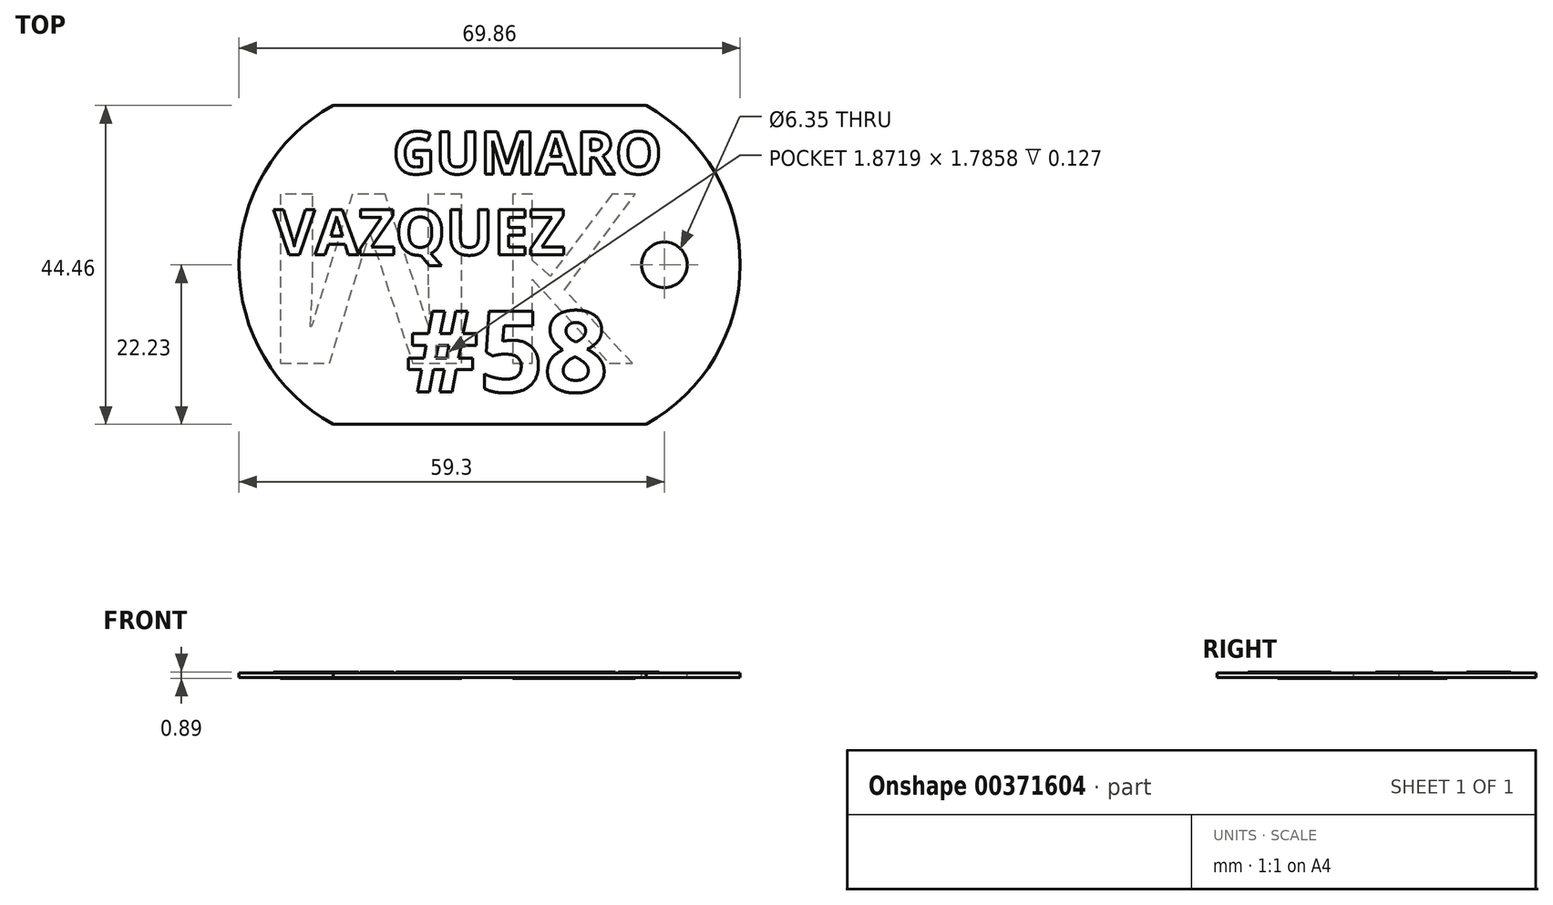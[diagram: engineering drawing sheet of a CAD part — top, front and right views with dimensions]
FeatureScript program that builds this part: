
annotation { "Feature Type Name" : "Feature", "Feature Type Description" : "" }
export const myFeature = defineFeature(function(context is Context, id is Id, definition is map)
    precondition{}
    {
        {
            var Q0;
            Q0=qCreatedBy(makeId("Top.planeOp"),FACE);
            var sketch = newSketch(context, id + "F0", { "sketchPlane" : qUnion([Q0])});
            skLineSegment(sketch, "E0.bottom", {"start": v(21.82, -22.22) * mm, "end": v(-21.82, -22.23) * mm});
            skLineSegment(sketch, "E0.top", {"start": v(21.82, 22.23) * mm, "end": v(-21.82, 22.23) * mm});
            skPoint(sketch, "E0.middle", {"position": v(0, 0) * mm});
            skArc(sketch, "E1", {"start": v(-21.82, 22.22) * mm, "mid": v(-34.93, 0) * mm, "end": v(-21.82, -22.23) * mm});
            skArc(sketch, "E2", {"start": v(21.82, -22.22) * mm, "mid": v(34.92, 0) * mm, "end": v(21.82, 22.23) * mm});
            skSolve(sketch);
        }
        {
            var Q0;
            Q0=makeQuery(id+"F0.imprint","IMPRINT",FACE,{"disambiguationData":[TD([[makeQuery(id+"F0.imprint","IMPRINT",EDGE,{"derivedFrom":sQuery(id+"F0.wireOp",EDGE,"E0.bottom")}),-1.0]])]});
            extrude(context, id + "F1", {"entities" : qUnion([Q0]), "depth" : 0.64 * mm});
        }
        {
            var Q0;
            Q0=makeQuery(id+"F1.opExtrude","CAP_FACE",FACE,{"disambiguationData":[OSD([sQuery(id+"F0.wireOp",EDGE,"E0.bottom"),sQuery(id+"F0.wireOp",EDGE,"E0.top"),sQuery(id+"F0.wireOp",EDGE,"E1"),sQuery(id+"F0.wireOp",EDGE,"E2")])],"isStart":false});
            var sketch = newSketch(context, id + "F2", { "sketchPlane" : qUnion([Q0])});
            skCircle(sketch, "E3", {"center": v(24.37, 0) * mm, "radius": 3.35 * mm});
            skSolve(sketch);
        }
        {
            var Q0;
            Q0=sQuery(id+"F2.wireOp",VERTEX,"E3.center");
            var Q1;
            Q1=makeQuery(id+"F1.opExtrude","SWEPT_BODY",BODY,{"disambiguationData":[OSD([sQuery(id+"F0.wireOp",EDGE,"E0.bottom"),sQuery(id+"F0.wireOp",EDGE,"E0.top"),sQuery(id+"F0.wireOp",EDGE,"E1"),sQuery(id+"F0.wireOp",EDGE,"E2")])]});
            hole(context, id + "F3", {"style" : HoleStyle.SIMPLE, "endStyle" : HoleEndStyle.THROUGH, "holeDiameter" : 6.35 * mm, "isTappedThrough" : true, "tappedDepth" : 12.7 * mm, "tapClearance" : 3, "locations" : qUnion([Q0]), "scope" : qUnion([Q1])});
        }
        {
            var Q0;
            Q0=makeQuery(id+"F1.opExtrude","CAP_FACE",FACE,{"disambiguationData":[OSD([sQuery(id+"F0.wireOp",EDGE,"E0.bottom"),sQuery(id+"F0.wireOp",EDGE,"E0.top"),sQuery(id+"F0.wireOp",EDGE,"E1"),sQuery(id+"F0.wireOp",EDGE,"E2")])],"isStart":false});
            var sketch = newSketch(context, id + "F4", { "sketchPlane" : qUnion([Q0])});
            skText(sketch, "E4", { "text": "GUMARO", "fontName": "OpenSans-Bold.ttf"});
            skText(sketch, "E5", { "text": "VAZQUEZ", "fontName": "OpenSans-Bold.ttf"});
            skText(sketch, "E6", { "text": "#58", "fontName": "OpenSans-Bold.ttf"});
            const initialGuessF4  = {"E4": [-0.01352, 0.01268, 1, 0, 0.00592], "E5": [-0.03008, 0.0014, 1, 0, 0.00635], "E6": [-0.01166, -0.0177, 1, 0, 0.01135]};
            skSetInitialGuess(sketch, initialGuessF4);
            skSolve(sketch);
        }
        {
            var Q0;
            Q0 = qSketchRegion(id + "F4", true);
            extrude(context, id + "F5", {"entities" : qUnion([Q0]), "operationType" : NewBodyOperationType.ADD, "depth" : 0.13 * mm});
        }
        {
            var Q0;
            Q0=makeQuery(id+"F1.opExtrude","CAP_FACE",FACE,{"disambiguationData":[OSD([sQuery(id+"F0.wireOp",EDGE,"E0.bottom"),sQuery(id+"F0.wireOp",EDGE,"E0.top"),sQuery(id+"F0.wireOp",EDGE,"E1"),sQuery(id+"F0.wireOp",EDGE,"E2")])],"isStart":true});
            var sketch = newSketch(context, id + "F6", { "sketchPlane" : qUnion([Q0])});
            skText(sketch, "E7", { "text": "M", "fontName": "OpenSans-Bold.ttf"});
            skText(sketch, "E8", { "text": "K", "fontName": "OpenSans-Regular.ttf"});
            const initialGuessF6  = {"E7": [-0.0321, -0.00987, 1, 0, 0.0238], "E8": [0, -0.00987, 1, 0, 0.0238]};
            skSetInitialGuess(sketch, initialGuessF6);
            skSolve(sketch);
        }
        {
            var Q0;
            Q0 = qSketchRegion(id + "F6", true);
            extrude(context, id + "F7", {"entities" : qUnion([Q0]), "operationType" : NewBodyOperationType.ADD, "depth" : 0.13 * mm});
        }
    });
